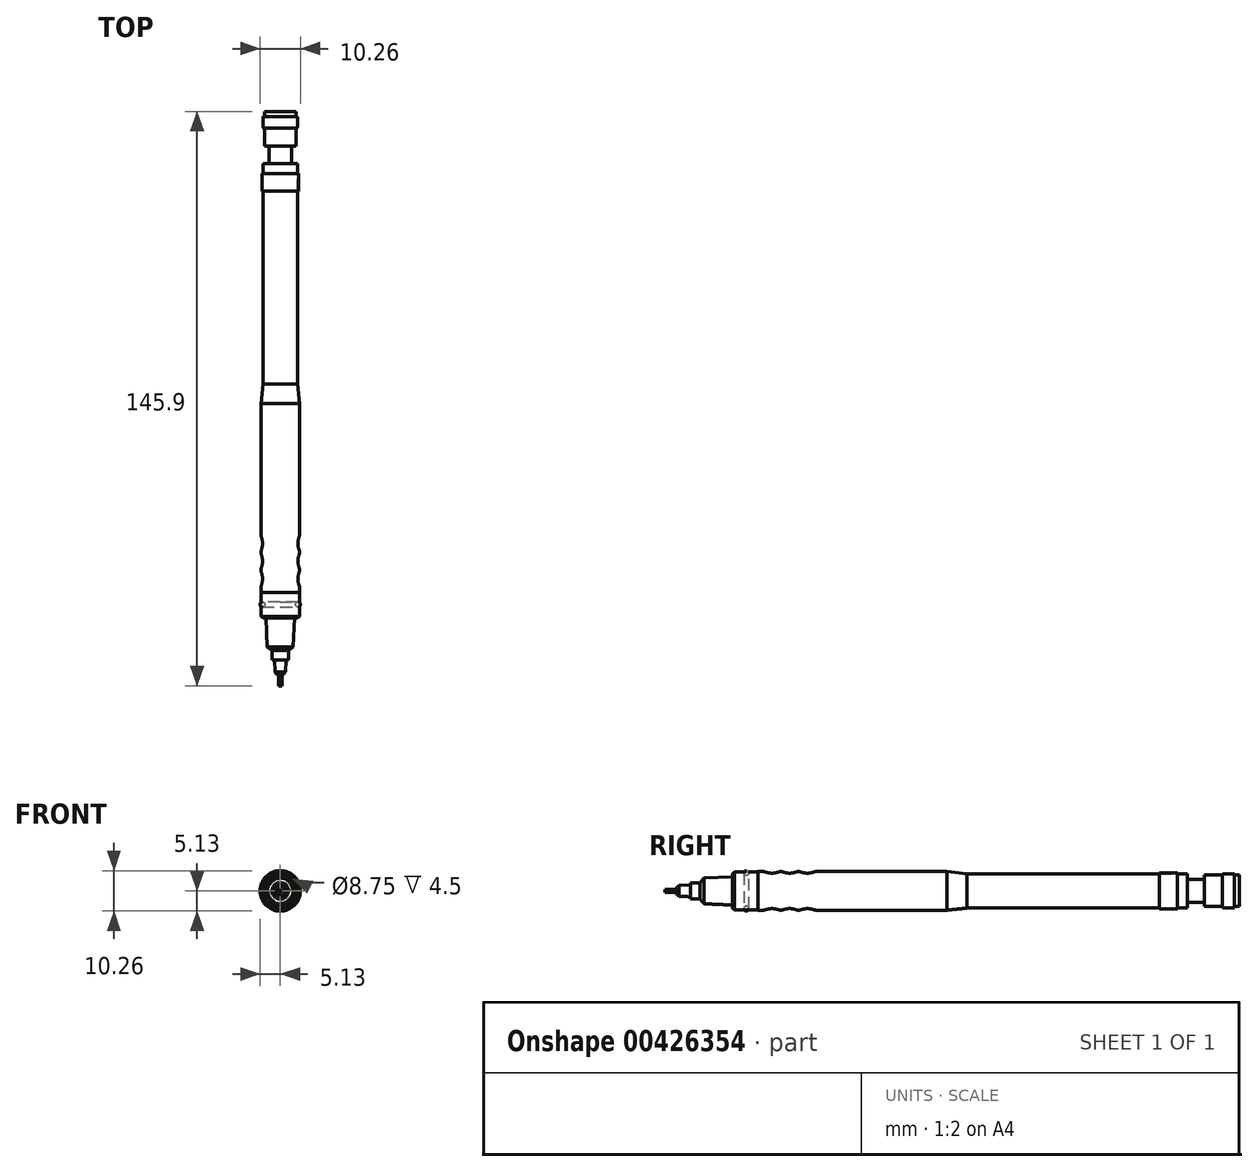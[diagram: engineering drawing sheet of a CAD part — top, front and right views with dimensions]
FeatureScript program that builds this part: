
annotation { "Feature Type Name" : "Feature", "Feature Type Description" : "" }
export const myFeature = defineFeature(function(context is Context, id is Id, definition is map)
    precondition{}
    {
        {
            var Q0;
            Q0=qCreatedBy(makeId("Front.planeOp"),FACE);
            var sketch = newSketch(context, id + "F0", { "sketchPlane" : qUnion([Q0])});
            skCircle(sketch, "E0", {"center": v(0, 0) * mm, "radius": 4.38 * mm});
            skSolve(sketch);
        }
        {
            var Q0;
            Q0 = qSketchRegion(id + "F0", true);
            extrude(context, id + "F1", {"entities" : qUnion([Q0]), "depth" : 56 * mm});
        }
        {
            var Q0;
            Q0=makeQuery(id+"F1.opExtrude","CAP_FACE",FACE,{"disambiguationData":[OSD([sQuery(id+"F0.wireOp",EDGE,"E0")])],"isStart":true});
            var sketch = newSketch(context, id + "F2", { "sketchPlane" : qUnion([Q0])});
            skCircle(sketch, "E1", {"center": v(0, 0) * mm, "radius": 2.88 * mm});
            skSolve(sketch);
        }
        {
            var Q0;
            Q0 = qSketchRegion(id + "F2", true);
            extrude(context, id + "F3", {"entities" : qUnion([Q0]), "depth" : 4.4 * mm});
        }
        {
            var Q0;
            Q0=makeQuery(id+"F3.opExtrude","CAP_FACE",FACE,{"disambiguationData":[OSD([sQuery(id+"F2.wireOp",EDGE,"E1")])],"isStart":false});
            var sketch = newSketch(context, id + "F4", { "sketchPlane" : qUnion([Q0])});
            skCircle(sketch, "E2", {"center": v(0, 0) * mm, "radius": 4 * mm});
            skSolve(sketch);
        }
        {
            var Q0;
            Q0 = qSketchRegion(id + "F4", true);
            extrude(context, id + "F5", {"entities" : qUnion([Q0]), "depth" : 4.6 * mm});
        }
        {
            var Q0;
            Q0=makeQuery(id+"F5.opExtrude","CAP_FACE",FACE,{"disambiguationData":[OSD([sQuery(id+"F4.wireOp",EDGE,"E2")])],"isStart":false});
            var sketch = newSketch(context, id + "F6", { "sketchPlane" : qUnion([Q0])});
            skCircle(sketch, "E3", {"center": v(0, 0) * mm, "radius": 4.35 * mm});
            skSolve(sketch);
        }
        {
            var Q0;
            Q0 = qSketchRegion(id + "F6", true);
            extrude(context, id + "F7", {"entities" : qUnion([Q0]), "depth" : 3 * mm});
        }
        {
            var Q0;
            Q0=makeQuery(id+"F7.opExtrude","CAP_FACE",FACE,{"disambiguationData":[OSD([sQuery(id+"F6.wireOp",EDGE,"E3")])],"isStart":false});
            var sketch = newSketch(context, id + "F8", { "sketchPlane" : qUnion([Q0])});
            skCircle(sketch, "E4", {"center": v(0, 0) * mm, "radius": 4 * mm});
            skSolve(sketch);
        }
        {
            var Q0;
            Q0 = qSketchRegion(id + "F8", true);
            extrude(context, id + "F9", {"entities" : qUnion([Q0]), "depth" : 1.25 * mm});
        }
        {
            var Q0;
            Q0=makeQuery(id+"F7.opExtrude","CAP_EDGE",EDGE,{"disambiguationData":[OSD([sQuery(id+"F6.wireOp",EDGE,"E3")])],"isStart":false});
            var Q1;
            Q1=makeQuery(id+"F7.opExtrude","CAP_EDGE",EDGE,{"disambiguationData":[OSD([sQuery(id+"F6.wireOp",EDGE,"E3")])],"isStart":true});
            fillet(context, id + "F10", {"entities" : qUnion([Q0, Q1]), "radius" : .25 * mm, "tangentPropagation" : true, "allowEdgeOverflow" : false});
        }
        {
            var Q0;
            Q0=makeQuery(id+"F1.opExtrude","CAP_FACE",FACE,{"disambiguationData":[OSD([sQuery(id+"F0.wireOp",EDGE,"E0")])],"isStart":false});
            var sketch = newSketch(context, id + "F11", { "sketchPlane" : qUnion([Q0])});
            skCircle(sketch, "E5", {"center": v(0, 0) * mm, "radius": 4.38 * mm});
            skSolve(sketch);
        }
        {
            var Q0;
            Q0 = qSketchRegion(id + "F11", true);
            extrude(context, id + "F12", {"entities" : qUnion([Q0]), "depth" : 5 * mm, "hasDraft" : true, "draftAngle" : 6 * degree});
        }
        {
            var Q0;
            Q0=makeQuery(id+"F12.opExtrude","CAP_FACE",FACE,{"disambiguationData":[OSD([sQuery(id+"F11.wireOp",EDGE,"E5")])],"isStart":false});
            var sketch = newSketch(context, id + "F13", { "sketchPlane" : qUnion([Q0])});
            skCircle(sketch, "E6", {"center": v(0, 0) * mm, "radius": 4.9 * mm});
            skSolve(sketch);
        }
        {
            var Q0;
            Q0 = qSketchRegion(id + "F13", true);
            extrude(context, id + "F14", {"entities" : qUnion([Q0]), "depth" : 48 * mm});
        }
        {
            var Q0;
            Q0=qCreatedBy(makeId("Right.planeOp"),FACE);
            var sketch = newSketch(context, id + "F15", { "sketchPlane" : qUnion([Q0])});
            skCircle(sketch, "E7", {"center": v(-105.5, 9.5) * mm, "radius": 5 * mm});
            skCircle(sketch, "E8.1.0.0", {"center": v(-101, 9.5) * mm, "radius": 5 * mm});
            skCircle(sketch, "E8.2.0.0", {"center": v(-96.5, 9.5) * mm, "radius": 5 * mm});
            skLineSegment(sketch, "E8.direction1", {"start": v(-105.5, 9.5) * mm, "end": v(-101, 9.5) * mm, "construction": true});
            skSolve(sketch);
        }
        {
            var Q0;
            Q0 = qSketchRegion(id + "F15", true);
            var Q1;
            Q1=makeQuery(id+"F14.opExtrude","CAP_EDGE",EDGE,{"disambiguationData":[OSD([sQuery(id+"F13.wireOp",EDGE,"E6")])],"isStart":false});
            revolve(context, id + "F16", {"operationType" : NewBodyOperationType.REMOVE, "entities" : qUnion([Q0]), "axis" : qUnion([Q1]), "revolveType" : RevolveType.FULL, "oppositeDirection" : true});
        }
        {
            var Q0;
            Q0=makeQuery(id+"F16.boolean.opBoolean","INTERSECT",EDGE,{"disambiguationData":[OD(1.0)],"derivedFrom":[makeQuery(id+"F14.opExtrude","SWEPT_FACE",FACE,{"disambiguationData":[OSD([sQuery(id+"F13.wireOp",EDGE,"E6")])]}),makeQuery(id+"F16.opRevolve","SWEPT_FACE",FACE,{"disambiguationData":[OSD([sQuery(id+"F15.wireOp",EDGE,"E7")])]})]});
            var Q1;
            {var subQ0=sQuery(id+"F15.wireOp",EDGE,"E8.1.0.0");Q1=makeQuery(id+"F16.boolean.opBoolean","INTERSECT",EDGE,{"disambiguationData":[OD(0.0)],"derivedFrom":[makeQuery(id+"F14.opExtrude","SWEPT_FACE",FACE,{"disambiguationData":[OSD([sQuery(id+"F13.wireOp",EDGE,"E6")])]}),makeQuery(id+"F16.opRevolve","SWEPT_FACE",FACE,{"disambiguationData":[OSD([subQ0]),TDD([makeQuery(id+"F15.imprint","IMPRINT",EDGE,{"disambiguationData":[TD([[makeQuery(id+"F15.imprint","INTERSECT",VERTEX,{"disambiguationData":[OD(1.0)],"derivedFrom":[sQuery(id+"F15.wireOp",EDGE,"E7"),subQ0]}),-1.0]])],"derivedFrom":subQ0})])]})]});}
            var Q2;
            {var subQ0=sQuery(id+"F15.wireOp",EDGE,"E8.1.0.0");Q2=makeQuery(id+"F16.boolean.opBoolean","INTERSECT",EDGE,{"disambiguationData":[OD(1.0)],"derivedFrom":[makeQuery(id+"F14.opExtrude","SWEPT_FACE",FACE,{"disambiguationData":[OSD([sQuery(id+"F13.wireOp",EDGE,"E6")])]}),makeQuery(id+"F16.opRevolve","SWEPT_FACE",FACE,{"disambiguationData":[OSD([subQ0]),TDD([makeQuery(id+"F15.imprint","IMPRINT",EDGE,{"disambiguationData":[TD([[makeQuery(id+"F15.imprint","INTERSECT",VERTEX,{"disambiguationData":[OD(1.0)],"derivedFrom":[sQuery(id+"F15.wireOp",EDGE,"E7"),subQ0]}),-1.0]])],"derivedFrom":subQ0})])]})]});}
            var Q3;
            Q3=makeQuery(id+"F16.boolean.opBoolean","INTERSECT",EDGE,{"disambiguationData":[OD(1.0)],"derivedFrom":[makeQuery(id+"F14.opExtrude","SWEPT_FACE",FACE,{"disambiguationData":[OSD([sQuery(id+"F13.wireOp",EDGE,"E6")])]}),makeQuery(id+"F16.opRevolve","SWEPT_FACE",FACE,{"disambiguationData":[OSD([sQuery(id+"F15.wireOp",EDGE,"E8.2.0.0")])]})]});
            var Q4;
            Q4=makeQuery(id+"F16.boolean.opBoolean","INTERSECT",EDGE,{"disambiguationData":[OD(0.0)],"derivedFrom":[makeQuery(id+"F14.opExtrude","SWEPT_FACE",FACE,{"disambiguationData":[OSD([sQuery(id+"F13.wireOp",EDGE,"E6")])]}),makeQuery(id+"F16.opRevolve","SWEPT_FACE",FACE,{"disambiguationData":[OSD([sQuery(id+"F15.wireOp",EDGE,"E8.2.0.0")])]})]});
            var Q5;
            Q5=makeQuery(id+"F16.boolean.opBoolean","INTERSECT",EDGE,{"disambiguationData":[OD(0.0)],"derivedFrom":[makeQuery(id+"F14.opExtrude","SWEPT_FACE",FACE,{"disambiguationData":[OSD([sQuery(id+"F13.wireOp",EDGE,"E6")])]}),makeQuery(id+"F16.opRevolve","SWEPT_FACE",FACE,{"disambiguationData":[OSD([sQuery(id+"F15.wireOp",EDGE,"E7")])]})]});
            fillet(context, id + "F17", {"entities" : qUnion([Q0, Q1, Q2, Q3, Q4, Q5]), "radius" : 1 * mm, "tangentPropagation" : true, "allowEdgeOverflow" : false});
        }
        {
            var Q0;
            Q0=makeQuery(id+"F14.opExtrude","CAP_FACE",FACE,{"disambiguationData":[OSD([sQuery(id+"F13.wireOp",EDGE,"E6")])],"isStart":false});
            var sketch = newSketch(context, id + "F18", { "sketchPlane" : qUnion([Q0])});
            skCircle(sketch, "E9", {"center": v(0, 0) * mm, "radius": 4.85 * mm});
            skSolve(sketch);
        }
        {
            var Q0;
            Q0 = qSketchRegion(id + "F18", true);
            extrude(context, id + "F19", {"entities" : qUnion([Q0]), "depth" : 6 * mm});
        }
        {
            var Q0;
            Q0=makeQuery(id+"F19.opExtrude","CAP_FACE",FACE,{"disambiguationData":[OSD([sQuery(id+"F18.wireOp",EDGE,"E9")])],"isStart":false});
            var sketch = newSketch(context, id + "F20", { "sketchPlane" : qUnion([Q0])});
            skCircle(sketch, "E10", {"center": v(0, 0) * mm, "radius": 4.85 * mm});
            skSolve(sketch);
        }
        {
            var Q0;
            Q0 = qSketchRegion(id + "F20", true);
            extrude(context, id + "F21", {"entities" : qUnion([Q0]), "operationType" : NewBodyOperationType.ADD, "depth" : .5 * mm, "hasDraft" : true, "draftAngle" : 45 * degree, "draftPullDirection" : true});
        }
        {
            var Q0;
            Q0=makeQuery(id+"F21.opExtrude","CAP_FACE",FACE,{"disambiguationData":[OSD([sQuery(id+"F20.wireOp",EDGE,"E10")])],"isStart":false});
            var sketch = newSketch(context, id + "F22", { "sketchPlane" : qUnion([Q0])});
            skCircle(sketch, "E11", {"center": v(0, 0) * mm, "radius": 3.6 * mm});
            skSolve(sketch);
        }
        {
            var Q0;
            Q0 = qSketchRegion(id + "F22", true);
            extrude(context, id + "F23", {"entities" : qUnion([Q0]), "operationType" : NewBodyOperationType.ADD, "depth" : 7.25 * mm, "hasDraft" : true, "draftAngle" : 2.5 * degree, "draftPullDirection" : true});
        }
        {
            var Q0;
            Q0=makeQuery(id+"F23.opExtrude","CAP_FACE",FACE,{"disambiguationData":[OSD([sQuery(id+"F22.wireOp",EDGE,"E11")])],"isStart":false});
            var sketch = newSketch(context, id + "F24", { "sketchPlane" : qUnion([Q0])});
            skCircle(sketch, "E12", {"center": v(0, 0) * mm, "radius": 3.28 * mm});
            skSolve(sketch);
        }
        {
            var Q0;
            Q0 = qSketchRegion(id + "F24", true);
            extrude(context, id + "F25", {"entities" : qUnion([Q0]), "operationType" : NewBodyOperationType.ADD, "depth" : 1 * mm, "hasDraft" : true, "draftAngle" : 50 * degree, "draftPullDirection" : true});
        }
        {
            var Q0;
            Q0=makeQuery(id+"F25.opExtrude","CAP_FACE",FACE,{"disambiguationData":[OSD([sQuery(id+"F24.wireOp",EDGE,"E12")])],"isStart":false});
            var sketch = newSketch(context, id + "F26", { "sketchPlane" : qUnion([Q0])});
            skCircle(sketch, "E13", {"center": v(0, 0) * mm, "radius": 2.1 * mm});
            skSolve(sketch);
        }
        {
            var Q0;
            Q0 = qSketchRegion(id + "F26", true);
            extrude(context, id + "F27", {"entities" : qUnion([Q0]), "operationType" : NewBodyOperationType.ADD, "depth" : 2.4 * mm});
        }
        {
            var Q0;
            Q0=makeQuery(id+"F27.opExtrude","CAP_FACE",FACE,{"disambiguationData":[OSD([sQuery(id+"F26.wireOp",EDGE,"E13")])],"isStart":false});
            var sketch = newSketch(context, id + "F28", { "sketchPlane" : qUnion([Q0])});
            skCircle(sketch, "E14", {"center": v(0, 0) * mm, "radius": 1.5 * mm});
            skSolve(sketch);
        }
        {
            var Q0;
            Q0 = qSketchRegion(id + "F28", true);
            extrude(context, id + "F29", {"entities" : qUnion([Q0]), "depth" : 3 * mm, "hasDraft" : true, "draftAngle" : 3 * degree, "draftPullDirection" : true});
        }
        {
            var Q0;
            Q0=makeQuery(id+"F29.opExtrude","CAP_FACE",FACE,{"disambiguationData":[OSD([sQuery(id+"F28.wireOp",EDGE,"E14")])],"isStart":false});
            var sketch = newSketch(context, id + "F30", { "sketchPlane" : qUnion([Q0])});
            skCircle(sketch, "E15", {"center": v(0, 0) * mm, "radius": 1.15 * mm});
            skSolve(sketch);
        }
        {
            var Q0;
            Q0 = qSketchRegion(id + "F30", true);
            extrude(context, id + "F31", {"entities" : qUnion([Q0]), "depth" : .5 * mm});
        }
        {
            var Q0;
            Q0=makeQuery(id+"F31.opExtrude","CAP_FACE",FACE,{"disambiguationData":[OSD([sQuery(id+"F30.wireOp",EDGE,"E15")])],"isStart":false});
            var sketch = newSketch(context, id + "F32", { "sketchPlane" : qUnion([Q0])});
            skCircle(sketch, "E16", {"center": v(0, 0) * mm, "radius": 0.43 * mm});
            skSolve(sketch);
        }
        {
            var Q0;
            Q0 = qSketchRegion(id + "F32", true);
            extrude(context, id + "F33", {"entities" : qUnion([Q0]), "operationType" : NewBodyOperationType.ADD, "depth" : 3 * mm});
        }
        {
            var Q0;
            Q0=qCreatedBy(makeId("Front.planeOp"),FACE);
            cPlane(context, id + "F34", {"entities" : qUnion([Q0]), "cplaneType" : CPlaneType.OFFSET, "offset" : 2.5 * mm, "width" : 150 * mm, "height" : 150 * mm});
        }
        {
            var Q0;
            Q0=qCreatedBy(id+"F34.planeOp",FACE);
            var sketch = newSketch(context, id + "F35", { "sketchPlane" : qUnion([Q0])});
            skCircle(sketch, "E17", {"center": v(0, 0) * mm, "radius": 4.38 * mm});
            skCircle(sketch, "E18", {"center": v(0, 0) * mm, "radius": 4.62 * mm});
            skSolve(sketch);
        }
        {
            var Q0;
            Q0 = qSketchRegion(id + "F35", true);
            extrude(context, id + "F36", {"entities" : qUnion([Q0]), "depth" : 4.5 * mm});
        }
        {
            var Q0;
            Q0=qCreatedBy(makeId("Right.planeOp"),FACE);
            var sketch = newSketch(context, id + "F37", { "sketchPlane" : qUnion([Q0])});
            skCircle(sketch, "E19", {"center": v(-112, 4.5) * mm, "radius": 0.62 * mm});
            skSolve(sketch);
        }
        {
            var Q0;
            Q0 = qSketchRegion(id + "F37", true);
            var Q1;
            Q1=makeQuery(id+"F19.opExtrude","SWEPT_FACE",FACE,{"disambiguationData":[OSD([sQuery(id+"F18.wireOp",EDGE,"E9")])]});
            revolve(context, id + "F38", {"entities" : qUnion([Q0]), "axis" : qUnion([Q1]), "revolveType" : RevolveType.FULL});
        }
    });
